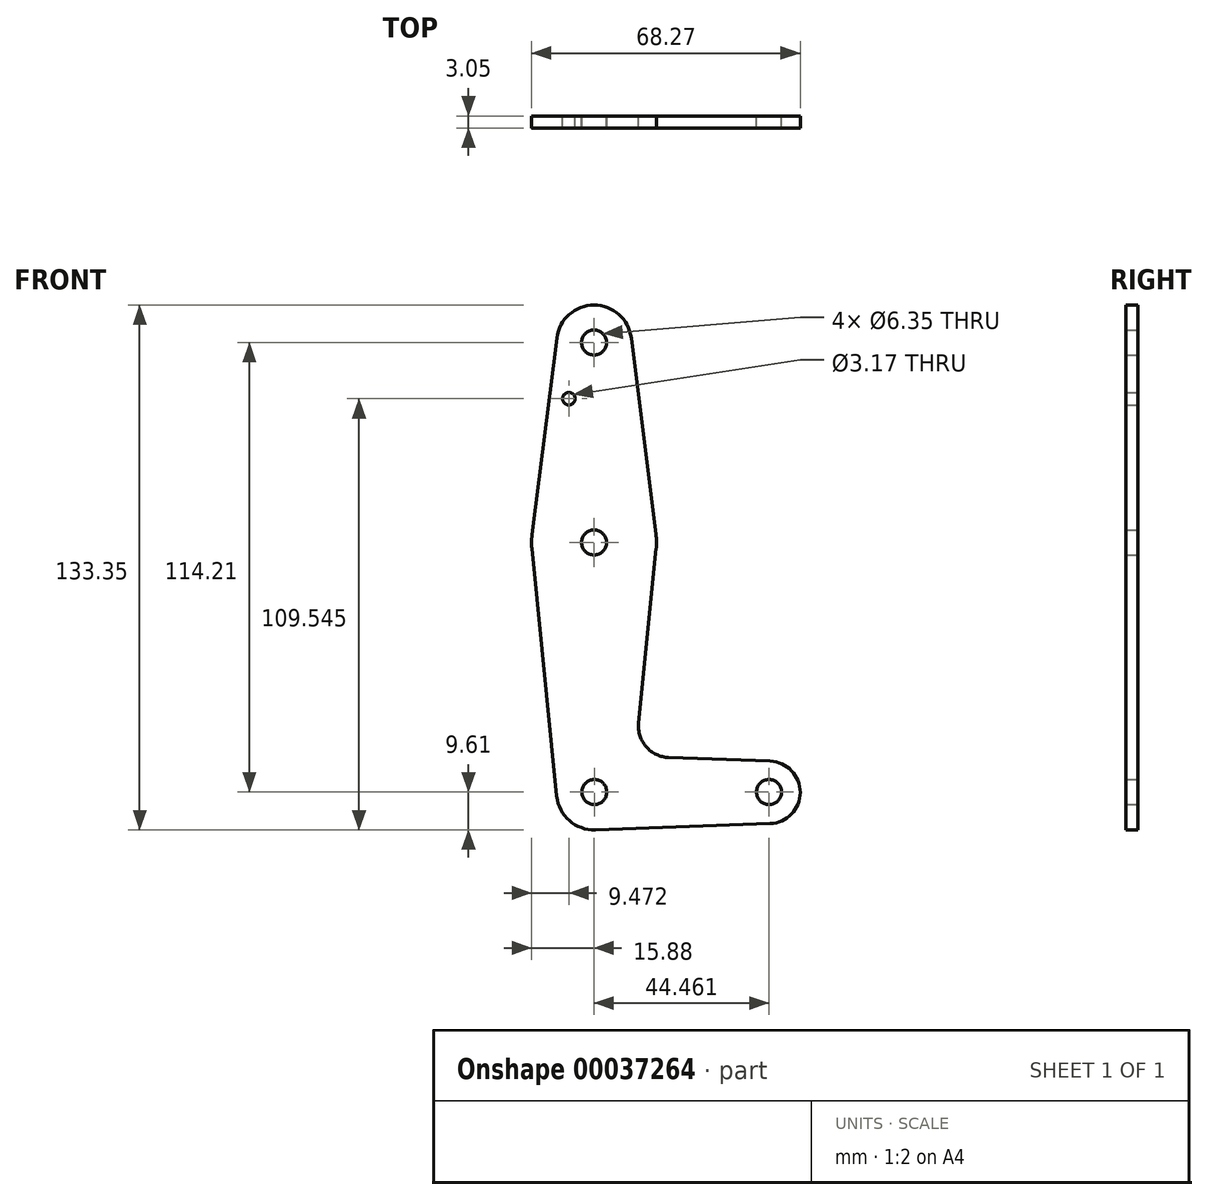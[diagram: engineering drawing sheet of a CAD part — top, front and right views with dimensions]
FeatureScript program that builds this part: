
annotation { "Feature Type Name" : "Feature", "Feature Type Description" : "" }
export const myFeature = defineFeature(function(context is Context, id is Id, definition is map)
    precondition{}
    {
        {
            var Q0;
            Q0=qCreatedBy(makeId("Front.planeOp"),FACE);
            var sketch = newSketch(context, id + "F0", { "sketchPlane" : qUnion([Q0])});
            skCircle(sketch, "E0", {"center": v(0, 0) * mm, "radius": 9.53 * mm});
            skCircle(sketch, "E1", {"center": v(0, 63.5) * mm, "radius": 15.88 * mm});
            skCircle(sketch, "E2", {"center": v(0, 114.3) * mm, "radius": 9.53 * mm});
            skCircle(sketch, "E3", {"center": v(44.45, 0) * mm, "radius": 7.94 * mm});
            skLineSegment(sketch, "E4", {"start": v(0, 114.3) * mm, "end": v(0, 0) * mm, "construction": true});
            skLineSegment(sketch, "E5", {"start": v(44.45, 0) * mm, "end": v(0, 0) * mm, "construction": true});
            skLineSegment(sketch, "E6", {"start": v(-9.45, 115.5) * mm, "end": v(-15.75, 65.48) * mm});
            skLineSegment(sketch, "E7", {"start": v(9.45, 115.5) * mm, "end": v(15.75, 65.48) * mm});
            skLineSegment(sketch, "E8", {"start": v(18.97, 8.85) * mm, "end": v(44.73, 7.93) * mm});
            skLineSegment(sketch, "E9", {"start": v(0.34, -9.52) * mm, "end": v(44.73, -7.93) * mm});
            skLineSegment(sketch, "E10", {"start": v(-15.8, 61.91) * mm, "end": v(-9.48, -0.95) * mm});
            skLineSegment(sketch, "E11", {"start": v(15.8, 61.91) * mm, "end": v(11.34, 17.6) * mm});
            skCircle(sketch, "E12", {"center": v(0, 114.3) * mm, "radius": 3.18 * mm});
            skCircle(sketch, "E13", {"center": v(0, 63.5) * mm, "radius": 3.18 * mm});
            skCircle(sketch, "E14", {"center": v(0.07, 0.09) * mm, "radius": 3.18 * mm});
            skCircle(sketch, "E15", {"center": v(44.46, 0.09) * mm, "radius": 3.18 * mm});
            skCircle(sketch, "E16", {"center": v(-6.4, 100.03) * mm, "radius": 1.59 * mm});
            skArc(sketch, "E17.filletArc", {"start": v(11.34, 17.6) * mm, "mid": v(13.26, 11.57) * mm, "end": v(18.97, 8.85) * mm});
            skSolve(sketch);
        }
        {
            var Q0;
            Q0 = qSketchRegion(id + "F0", true);
            extrude(context, id + "F1", {"entities" : qUnion([Q0]), "depth" : 3.05 * mm});
        }
    });
